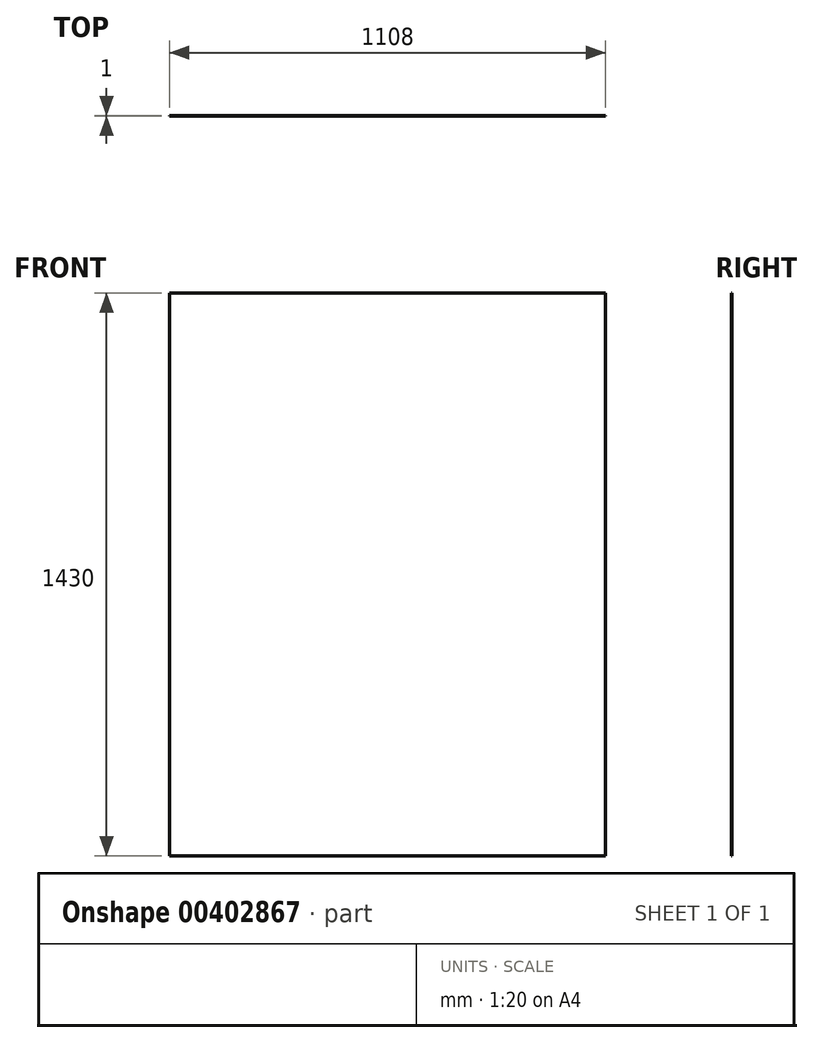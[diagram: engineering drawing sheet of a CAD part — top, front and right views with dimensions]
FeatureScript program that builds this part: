
annotation { "Feature Type Name" : "Feature", "Feature Type Description" : "" }
export const myFeature = defineFeature(function(context is Context, id is Id, definition is map)
    precondition{}
    {
        {
            var Q0;
            Q0=qCreatedBy(makeId("Front.planeOp"),FACE);
            var sketch = newSketch(context, id + "F0", { "sketchPlane" : qUnion([Q0])});
            skLineSegment(sketch, "E0.bottom", {"start": v(-554, 715) * mm, "end": v(554, 715) * mm});
            skLineSegment(sketch, "E0.top", {"start": v(-554, -715) * mm, "end": v(554, -715) * mm});
            skLineSegment(sketch, "E0.left", {"start": v(-554, 715) * mm, "end": v(-554, -715) * mm});
            skLineSegment(sketch, "E0.right", {"start": v(554, 715) * mm, "end": v(554, -715) * mm});
            skPoint(sketch, "E0.middle", {"position": v(0, 0) * mm});
            skSolve(sketch);
        }
        {
            var Q0;
            Q0=makeQuery(id+"F0.imprint","IMPRINT",FACE,{"disambiguationData":[TD([[makeQuery(id+"F0.imprint","IMPRINT",EDGE,{"derivedFrom":sQuery(id+"F0.wireOp",EDGE,"E0.bottom")}),-1.0]])]});
            extrude(context, id + "F1", {"entities" : qUnion([Q0]), "depth" : 1 * mm});
        }
    });
